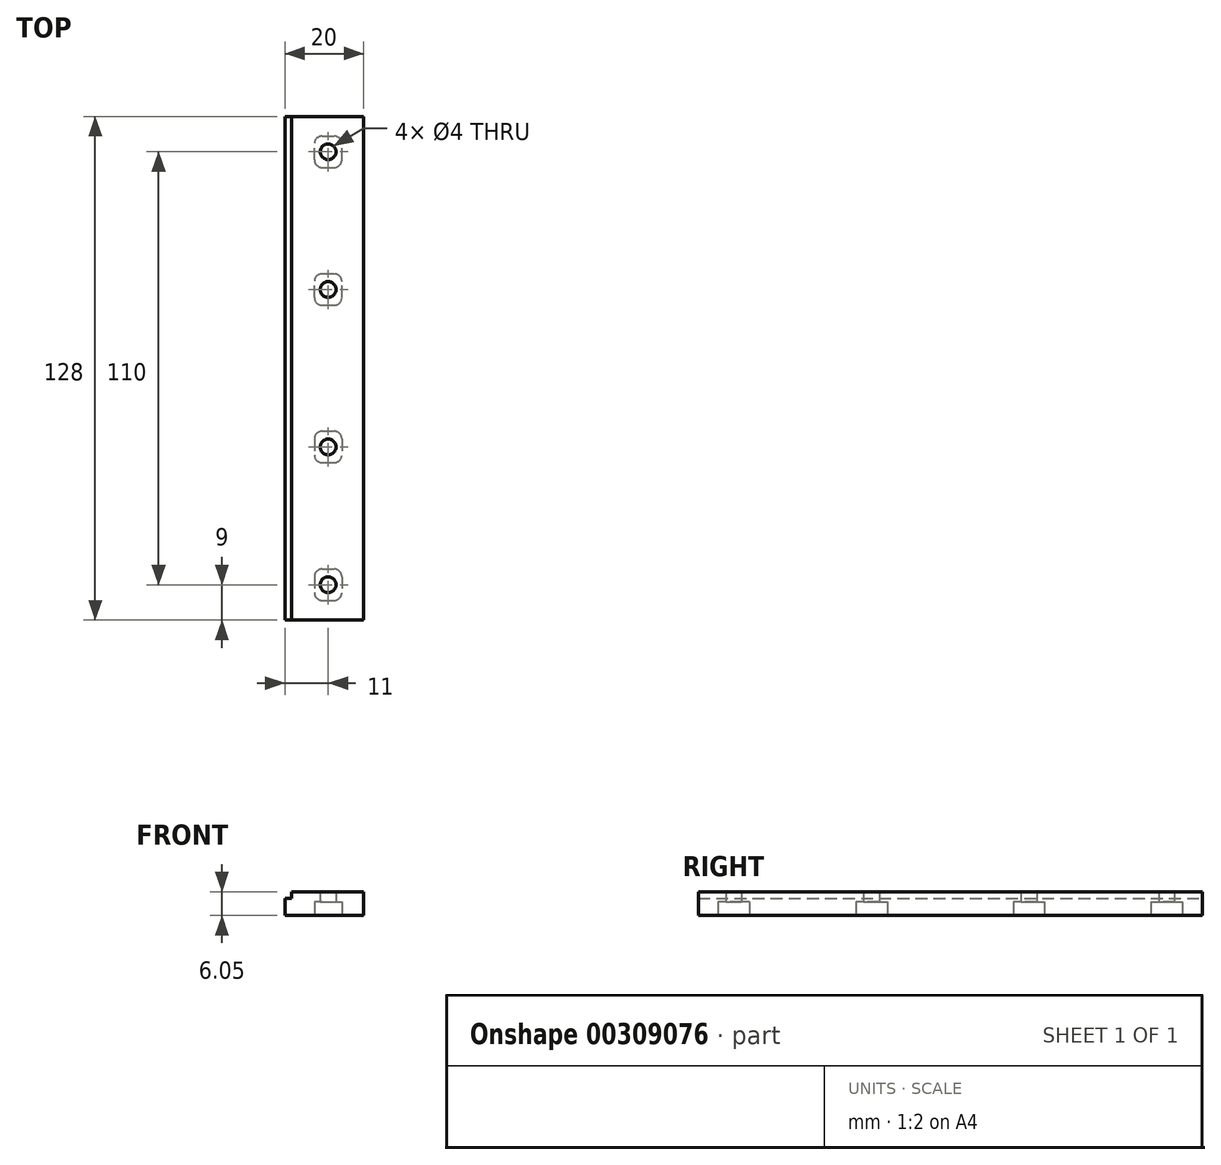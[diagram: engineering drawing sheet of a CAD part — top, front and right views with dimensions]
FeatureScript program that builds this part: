
annotation { "Feature Type Name" : "Feature", "Feature Type Description" : "" }
export const myFeature = defineFeature(function(context is Context, id is Id, definition is map)
    precondition{}
    {
        {
            var Q0;
            Q0=qCreatedBy(makeId("Front.planeOp"),FACE);
            var sketch = newSketch(context, id + "F0", { "sketchPlane" : qUnion([Q0])});
            skLineSegment(sketch, "E0.right", {"start": v(44.83, 0) * mm, "end": v(44.83, 6.05) * mm});
            skLineSegment(sketch, "E1", {"start": v(24.83, 0) * mm, "end": v(44.83, 0) * mm});
            skLineSegment(sketch, "E2", {"start": v(26.58, 6.05) * mm, "end": v(26.58, 4.3) * mm});
            skLineSegment(sketch, "E3", {"start": v(26.58, 4.3) * mm, "end": v(24.83, 4.3) * mm});
            skLineSegment(sketch, "E4", {"start": v(24.83, 4.3) * mm, "end": v(24.83, 0) * mm});
            skLineSegment(sketch, "E5", {"start": v(26.58, 6.05) * mm, "end": v(44.83, 6.05) * mm});
            skSolve(sketch);
        }
        {
            var Q0;
            Q0 = qSketchRegion(id + "F0", true);
            extrude(context, id + "F1", {"entities" : qUnion([Q0]), "depth" : 128 * mm});
        }
        {
            var Q0;
            Q0=makeQuery(id+"F1.opExtrude","SWEPT_FACE",FACE,{"disambiguationData":[OSD([sQuery(id+"F0.wireOp",EDGE,"E1")])]});
            var sketch = newSketch(context, id + "F2", { "sketchPlane" : qUnion([Q0])});
            skLineSegment(sketch, "E6", {"start": v(44.83, 64) * mm, "end": v(13.63, 64) * mm, "construction": true});
            skPoint(sketch, "E7", {"position": v(35.83, 119) * mm});
            skPoint(sketch, "E8.cornerSnap0", {"position": v(34.83, 128) * mm});
            skLineSegment(sketch, "E9.bottom", {"start": v(34.33, 115) * mm, "end": v(37.33, 115) * mm});
            skLineSegment(sketch, "E9.top", {"start": v(34.33, 123) * mm, "end": v(37.33, 123) * mm});
            skLineSegment(sketch, "E9.left", {"start": v(32.33, 117) * mm, "end": v(32.33, 121) * mm});
            skLineSegment(sketch, "E9.right", {"start": v(39.33, 117) * mm, "end": v(39.33, 121) * mm});
            skPoint(sketch, "E10", {"position": v(35.83, 84) * mm});
            skLineSegment(sketch, "E11.bottom", {"start": v(34.33, 80) * mm, "end": v(37.33, 80) * mm});
            skLineSegment(sketch, "E11.top", {"start": v(34.33, 88) * mm, "end": v(37.33, 88) * mm});
            skLineSegment(sketch, "E11.left", {"start": v(32.33, 82) * mm, "end": v(32.33, 86) * mm});
            skLineSegment(sketch, "E11.right", {"start": v(39.33, 82) * mm, "end": v(39.33, 86) * mm});
            skPoint(sketch, "E12.visualSharp", {"position": v(39.33, 123) * mm});
            skArc(sketch, "E12.filletArc", {"start": v(39.33, 121) * mm, "mid": v(38.74, 122.41) * mm, "end": v(37.33, 123) * mm});
            skPoint(sketch, "E13.visualSharp", {"position": v(39.33, 115) * mm});
            skArc(sketch, "E13.filletArc", {"start": v(37.33, 115) * mm, "mid": v(38.74, 115.59) * mm, "end": v(39.33, 117) * mm});
            skPoint(sketch, "E14.visualSharp", {"position": v(32.33, 115) * mm});
            skArc(sketch, "E14.filletArc", {"start": v(32.33, 117) * mm, "mid": v(32.92, 115.59) * mm, "end": v(34.33, 115) * mm});
            skPoint(sketch, "E15.visualSharp", {"position": v(32.33, 123) * mm});
            skArc(sketch, "E15.filletArc", {"start": v(34.33, 123) * mm, "mid": v(32.92, 122.41) * mm, "end": v(32.33, 121) * mm});
            skPoint(sketch, "E16.visualSharp", {"position": v(39.33, 88) * mm});
            skArc(sketch, "E16.filletArc", {"start": v(39.33, 86) * mm, "mid": v(38.74, 87.41) * mm, "end": v(37.33, 88) * mm});
            skPoint(sketch, "E17.visualSharp", {"position": v(32.33, 88) * mm});
            skArc(sketch, "E17.filletArc", {"start": v(34.33, 88) * mm, "mid": v(32.92, 87.41) * mm, "end": v(32.33, 86) * mm});
            skPoint(sketch, "E18.visualSharp", {"position": v(39.33, 80) * mm});
            skArc(sketch, "E18.filletArc", {"start": v(37.33, 80) * mm, "mid": v(38.74, 80.59) * mm, "end": v(39.33, 82) * mm});
            skPoint(sketch, "E19.visualSharp", {"position": v(32.33, 80) * mm});
            skArc(sketch, "E19.filletArc", {"start": v(32.33, 82) * mm, "mid": v(32.92, 80.59) * mm, "end": v(34.33, 80) * mm});
            skPoint(sketch, "E20.MirrorP", {"position": v(35.83, 9) * mm});
            skArc(sketch, "E21.MirrorCS", {"start": v(39.33, 42) * mm, "mid": v(38.74, 40.59) * mm, "end": v(37.33, 40) * mm});
            skArc(sketch, "E22.MirrorCS", {"start": v(34.33, 40) * mm, "mid": v(32.92, 40.59) * mm, "end": v(32.33, 42) * mm});
            skArc(sketch, "E23.MirrorCS", {"start": v(37.33, 48) * mm, "mid": v(38.74, 47.41) * mm, "end": v(39.33, 46) * mm});
            skArc(sketch, "E24.MirrorCS", {"start": v(39.33, 7) * mm, "mid": v(38.74, 5.59) * mm, "end": v(37.33, 5) * mm});
            skArc(sketch, "E25.MirrorCS", {"start": v(37.33, 13) * mm, "mid": v(38.74, 12.41) * mm, "end": v(39.33, 11) * mm});
            skArc(sketch, "E26.MirrorCS", {"start": v(32.33, 11) * mm, "mid": v(32.92, 12.41) * mm, "end": v(34.33, 13) * mm});
            skArc(sketch, "E27.MirrorCS", {"start": v(34.33, 5) * mm, "mid": v(32.92, 5.59) * mm, "end": v(32.33, 7) * mm});
            skPoint(sketch, "E28.MirrorP", {"position": v(35.83, 44) * mm});
            skArc(sketch, "E29.MirrorCS", {"start": v(32.33, 46) * mm, "mid": v(32.92, 47.41) * mm, "end": v(34.33, 48) * mm});
            skPoint(sketch, "E30.MirrorP", {"position": v(39.33, 40) * mm});
            skPoint(sketch, "E31.MirrorP", {"position": v(39.33, 5) * mm});
            skLineSegment(sketch, "E32.MirrorCS", {"start": v(34.33, 13) * mm, "end": v(37.33, 13) * mm});
            skLineSegment(sketch, "E33.MirrorCS", {"start": v(34.33, 5) * mm, "end": v(37.33, 5) * mm});
            skLineSegment(sketch, "E34.MirrorCS", {"start": v(32.33, 11) * mm, "end": v(32.33, 7) * mm});
            skLineSegment(sketch, "E35.MirrorCS", {"start": v(39.33, 11) * mm, "end": v(39.33, 7) * mm});
            skPoint(sketch, "E36.MirrorP", {"position": v(32.33, 48) * mm});
            skLineSegment(sketch, "E37.MirrorCS", {"start": v(34.33, 48) * mm, "end": v(37.33, 48) * mm});
            skLineSegment(sketch, "E38.MirrorCS", {"start": v(34.33, 40) * mm, "end": v(37.33, 40) * mm});
            skLineSegment(sketch, "E39.MirrorCS", {"start": v(39.33, 46) * mm, "end": v(39.33, 42) * mm});
            skLineSegment(sketch, "E40.MirrorCS", {"start": v(32.33, 46) * mm, "end": v(32.33, 42) * mm});
            skPoint(sketch, "E41.MirrorP", {"position": v(32.33, 40) * mm});
            skPoint(sketch, "E42.MirrorP", {"position": v(32.33, 13) * mm});
            skPoint(sketch, "E43.MirrorP", {"position": v(39.33, 13) * mm});
            skPoint(sketch, "E44.MirrorP", {"position": v(32.33, 5) * mm});
            skPoint(sketch, "E45.MirrorP", {"position": v(39.33, 48) * mm});
            skSolve(sketch);
        }
        {
            var Q0;
            Q0 = qSketchRegion(id + "F2", true);
            extrude(context, id + "F3", {"entities" : qUnion([Q0]), "operationType" : NewBodyOperationType.REMOVE, "oppositeDirection" : true, "depth" : 3.5 * mm});
        }
        {
            var Q0;
            Q0=makeQuery(id+"F1.opExtrude","SWEPT_FACE",FACE,{"disambiguationData":[OSD([sQuery(id+"F0.wireOp",EDGE,"E1")])]});
            var sketch = newSketch(context, id + "F4", { "sketchPlane" : qUnion([Q0])});
            skPoint(sketch, "E46", {"position": v(35.83, 119) * mm});
            skPoint(sketch, "E46.positionSnap0", {"position": v(32.33, 119) * mm});
            skPoint(sketch, "E46.positionSnap1", {"position": v(35.83, 123) * mm});
            skPoint(sketch, "E47", {"position": v(35.83, 84) * mm});
            skPoint(sketch, "E47.positionSnap0", {"position": v(32.33, 84) * mm});
            skPoint(sketch, "E47.positionSnap1", {"position": v(35.83, 88) * mm});
            skLineSegment(sketch, "E48", {"start": v(44.83, 64) * mm, "end": v(24.83, 64) * mm, "construction": true});
            skCircle(sketch, "E49", {"center": v(35.83, 119) * mm, "radius": 2 * mm});
            skCircle(sketch, "E50", {"center": v(35.83, 84) * mm, "radius": 2 * mm});
            skCircle(sketch, "E51.MirrorC", {"center": v(35.83, 44) * mm, "radius": 2 * mm});
            skCircle(sketch, "E52.MirrorC", {"center": v(35.83, 9) * mm, "radius": 2 * mm});
            skSolve(sketch);
        }
        {
            var Q0;
            Q0 = qSketchRegion(id + "F4", true);
            extrude(context, id + "F5", {"entities" : qUnion([Q0]), "operationType" : NewBodyOperationType.REMOVE, "endBound" : BoundingType.THROUGH_ALL, "oppositeDirection" : true, "depth" : 25 * mm});
        }
    });
